# Revit family: PRD_FrankeWS_TltRllHldrs_EXOSDoubleToiletRollHolder_EXOS676X_676B_676W
name_source: partatom
category: Specialty Equipment
revit_build: Autodesk Revit 2018 (Build: 20190510_1515(x64)
units: mm (PartAtom-declared; Revit-internal decimal feet)

## family parameters
Cut with Voids When Loaded = No
Host = Face
OmniClass Number = 23.40.20.21.21
OmniClass Title = Toilet Paper Dispensers
Part Type = Normal
Room Calculation Point = No
Round Connector Dimension = Use Diameter
Shared = No

## types (3) — shared parameters
AssetType = Fixed
Category = Pr_40_20_76_88, Toilet roll holders
Default Elevation = 1200 mm
DispenserMaterial = PRD_AR_StainlessSteel_SatinFinished
DurationUnit = year
Features = stainless steel, surface satin finished
FillingQuantity = 2
FillingQuantityUom = Rolls
Finish = satin finished
IfcExportAs = IfcFurnitureType
IfcExportType = USERDEFINED
IntegralAccessories = incl. mounting materials
IsBuiltIn = TRUE
Lock = Key-lock
MainColor = stainless steel
Manufacturer = KWC Group AG
ManufacturerName = KWC Group AG
ManufacturerURL = www.kwc.com
Material = stainless steel
MaterialCode = 1.4301
MaterialThickness = 1.20 mm
MaximumDepthDiameterOfConsumable = 120.00 mm
MaximumWidthOfConsumable = 100.00 mm
NBSDescription = Toilet roll holders
NBSReference = 45-35-72/368
NominalDepth = 147 mm  [stored 0.482283 ft]
NominalHeight = 193 mm  [stored 0.633202 ft]
NominalWidth = 280 mm  [stored 0.918635 ft]
ProductInformation = https://pim.kwc.com
Size = 280 x 193 x 147 mm
Spindle = Yes
Style = Roll holder
SurfaceTreatment = InoxPlus (anti fingerprint)
ToiletRollMaterial = PRD_AR_ToiletRoll
TypeOfFixing = Screw
TypeOfMounting = Wall mounting
URL = www.kwc.com
Uniclass2015Code = Pr_40_20_76_88
Uniclass2015Title = Toilet roll holders
Uniclass2015Version = Products v1.17
Version = 1
WarrantyDurationUnit = year

## per-type parameters (varying)
| type | BIMObjectName | Description | GrossWeight | ModelNumber | Name | NetWeight | PanelMaterial |
| EXOS676X | PRD_AR_ToiletRollHolders_EXOSDoubleToiletRollHolder_EXOS676X | Double toilet roll holder with spindle system for wall mounting, stainless steel with satin finish and InoxPlus surface refinement for the reduction of finger marks and better cleaning characteristics (easy to clean), material thickness 1.2 mm, closed casing, for two rolls with a maximum diameter of 120 mm, when the first roll is used up, the hidden spare roll is released by sliding the bottom cover on the opposite side, includes mounting materials. | 3.90 kg | 2030033180 | Double toilet roll holder EXOS676X | 3.09 kg | PRD_AR_StainlessSteel_SatinFinished |
| EXOS676B | PRD_AR_ToiletRollHolders_EXOSDoubleToiletRollHolder_EXOS676B | Double toilet roll holder with spindle system for wall mounting, stainless steel with satin finish, black safety glass front panel and casing with InoxPlus surface refinement for the reduction of finger marks and better cleaning characteristics (easy to clean), material thickness 1.2 mm, closed casing, for two rolls with a maximum diameter of 120 mm, when the first roll is used up, the hidden spare roll is released by sliding the bottom cover on the opposite side, includes mounting materials. | 4.37 kg | 2030034645 | Double toilet roll holder EXOS676B | 3.49 kg | PRD_AR_Glass_Black |
| EXOS676W | PRD_AR_ToiletRollHolders_EXOSDoubleToiletRollHolder_EXOS676W | Double toilet roll holder with spindle system for wall mounting, stainless steel with satin finish, white safety glass front panel and casing with InoxPlus surface refinement for the reduction of finger marks and better cleaning characteristics (easy to clean), material thickness 1.2 mm, closed casing, for two rolls with a maximum diameter of 120 mm, when the first roll is used up, the hidden spare roll is released by sliding the bottom cover on the opposite side, includes mounting materials. | 4.37 kg | 2030034670 | Double toilet roll holder EXOS676W | 3.49 kg | PRD_AR_Glass_White |

note: column(s) folded — value = type name in every type: Model, ModelReference

note: [stored X ft] marks values corroborated as IEEE doubles in the binary element streams (Revit-internal decimal feet)

## geometry (parser evidence)
native form markers: Sweep x6
no freeform markers — native parametric forms only
